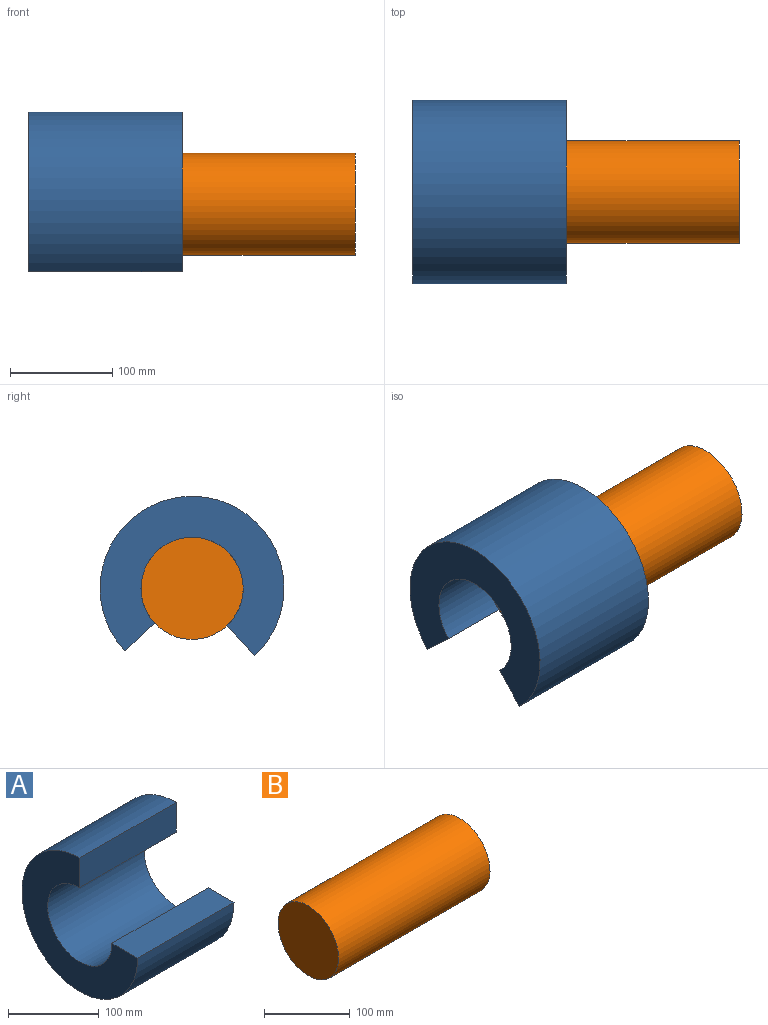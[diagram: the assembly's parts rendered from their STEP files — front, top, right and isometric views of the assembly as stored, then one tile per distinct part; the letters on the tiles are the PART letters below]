
ASSEMBLY  parts=2 mates=1
PART A: 6 faces, bbox 150x180x180 mm
  f0: cylinder r=50mm len=150mm, axis (1,0,0), area 35342.9mm2, adj f1,f3,f4,f5
  f1: plane 180x180mm, normal (1,0,0), area 13194.7mm2, adj f0,f2,f4,f5
  f2: cylinder r=90mm len=180mm, axis (1,0,0), area 63617.3mm2, adj f1,f3,f4,f5
  f3: plane 180x180mm, normal (-1,0,0), area 13194.7mm2, adj f0,f2,f4,f5
  f4: plane 150x40mm, normal (0,0,1), area 6000mm2, adj f0,f1,f2,f3
  f5: plane 150x40mm, normal (0,-1,0), area 6000mm2, adj f0,f1,f2,f3
PART B: 3 faces, bbox 250x100x100 mm
  f0: plane 100x100mm, normal (1,0,0), area 7854mm2, adj f1
  f1: cylinder r=50mm len=250mm, axis (-1,0,0), area 78539.8mm2, adj f0,f2
  f2: plane 100x100mm, normal (-1,0,0), area 7854mm2, adj f1
PLACE A rot(axis=(1,0,0),137deg) t=(-169.41,-34.07,-36.59)mm
PLACE B at identity fixed
MATE cylindrical A.f0 <-> B.f1  axis (1,0,0) through (-244.41,0,0)mm
